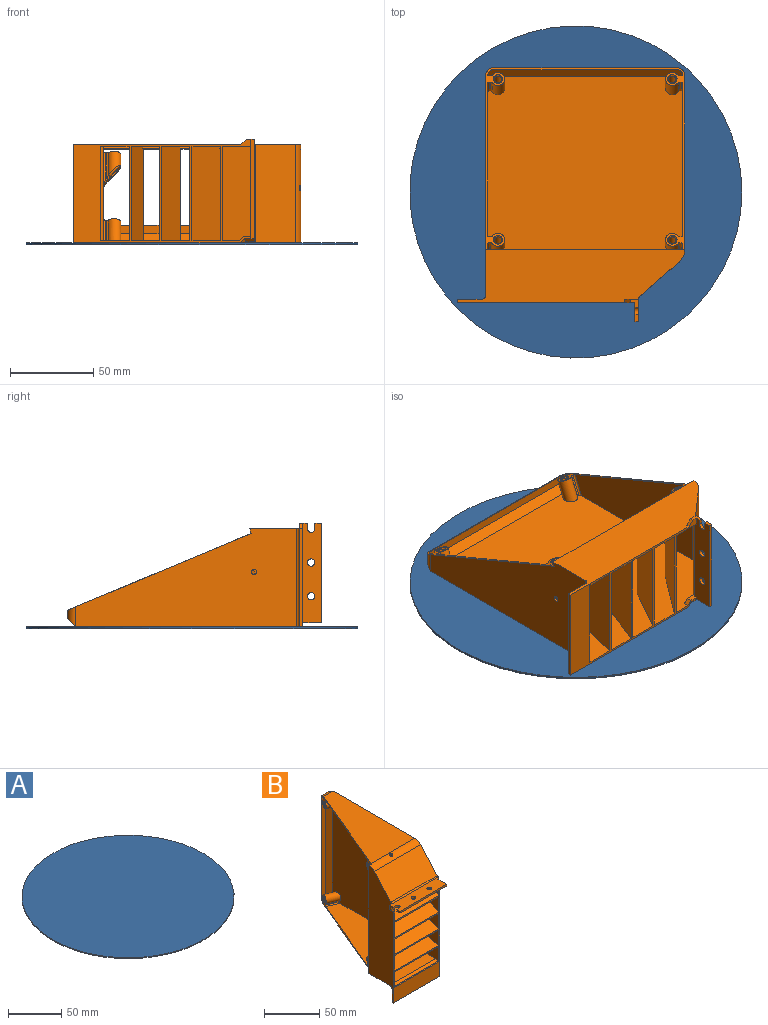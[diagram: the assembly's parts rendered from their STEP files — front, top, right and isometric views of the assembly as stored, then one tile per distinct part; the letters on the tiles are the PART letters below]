
ASSEMBLY  parts=2 mates=1
PART A: 3 faces, bbox 200x200x1 mm
  f0: cylinder r=100mm len=200mm, axis (0,0,-1), area 628.3mm2, adj f1,f2
  f1: plane 200x200mm, normal (0,0,1), area 31415.9mm2, adj f0
  f2: plane 200x200mm, normal (0,0,-1), area 31415.9mm2, adj f0
PART B: 134 faces, bbox 66.3x155.3x139.3 mm
  f0: plane 137.39x136.94mm, normal (1,0,0), area 15946.5mm2, adj f2,f23,f25,f38,f40,f42,f43,f44
  f1: plane 137x32mm, normal (-1,0,0), area 3430.7mm2, adj f2,f24,f26,f38,f39,f40,f42,f43
  f2: cylinder r=10mm len=59.06mm, axis (-1,0,0), area 492.2mm2, adj f0,f1,f22,f24,f25,f43,f132
  f3: cylinder r=8.8mm len=56.66mm, axis (-1,0,0), area 387.3mm2, adj f4,f5,f18,f22,f49,f53,f54,f58
  f4: plane 45.63x30.2mm, normal (1,0,0), area 599.4mm2, adj f3,f21,f37,f38,f51,f53,f58,f59
  f5: plane 138.4x121.59mm, normal (-1,0,0), area 15229.2mm2, adj f3,f17,f18,f19,f20,f38,f52,f56
  f6: plane 23.3x1.11mm, normal (0.92,-0.39,0), area 27.1mm2, adj f7,f24,f119,f127
  f7: plane 22.81x1.08mm, normal (-0.39,-0.92,0), area 26.4mm2, adj f6,f14,f119,f127
  f8: plane 34.04x30.2mm, normal (1,0,0), area 597.4mm2, adj f13,f38,f118,f124
  f9: plane 21.7x1.11mm, normal (0.92,-0.39,0), area 25.6mm2, adj f10,f24,f121,f123
  f10: plane 21.45x1.08mm, normal (-0.39,-0.92,0), area 25mm2, adj f9,f11,f121,f123
  f11: plane 30.2x28.5mm, normal (1,0,0), area 579.1mm2, adj f10,f38,f121,f123
  f12: plane 23.09x1.11mm, normal (0.92,-0.39,0), area 27.1mm2, adj f13,f24,f118,f124
  f13: plane 22.72x1.08mm, normal (-0.39,-0.92,0), area 26.4mm2, adj f8,f12,f118,f124
  f14: plane 39.59x30.2mm, normal (1,0,0), area 597.4mm2, adj f7,f38,f119,f127
  f15: plane 22.67x1.11mm, normal (0.92,-0.39,0), area 27.1mm2, adj f16,f17,f24,f120
  f16: plane 22.52x1.08mm, normal (-0.39,-0.92,0), area 26.3mm2, adj f15,f17,f50,f120
  f17: plane 128.03x56.82mm, normal (0,0,1), area 4787.5mm2, adj f5,f15,f16,f22,f50,f61,f82,f86
  f18: plane 99.87x51.06mm, normal (0,0,-1), area 3232.8mm2, adj f3,f5,f22,f94,f96
  f19: plane 8.51x3.56mm, normal (0,0,1), area 15mm2, adj f5,f60,f62,f84
  f20: plane 8.51x3.56mm, normal (0,0,-1), area 15mm2, adj f5,f60,f63,f98
  f21: plane 54.12x0.8mm, normal (0,1,0), area 43.3mm2, adj f4,f37,f51,f55
  f22: plane 120.88x111.58mm, normal (-0.92,0.39,0), area 597.5mm2, adj f2,f3,f17,f18,f24,f25,f41,f42
  f23: plane 5.65x0.54mm, normal (0,-1,0), area 2.9mm2, adj f0,f44,f129,f130
  f24: plane 120x2.75mm, normal (0.39,0.92,0), area 356.8mm2, adj f1,f2,f6,f9,f12,f15,f22,f42
  f25: plane 104.56x55.83mm, normal (0,0,1), area 3550.9mm2, adj f0,f2,f22,f48
  f26: plane 8.1x3.18mm, normal (0,1,0), area 20.7mm2, adj f1,f31,f36,f39
  f27: plane 3.18x2mm, normal (0,1,0), area 6.4mm2, adj f28,f35,f36,f37
  f28: plane 4.14x2mm, normal (-1,0,0), area 8.3mm2, adj f27,f29,f36,f37
  f29: plane 59.69x2mm, normal (0,-1,0), area 119.4mm2, adj f28,f30,f36,f37
  f30: plane 11.43x2mm, normal (1,0,0), area 22.9mm2, adj f29,f36,f37,f130
  f31: plane 4.92x4.87mm, normal (-1,0,0), area 15.6mm2, adj f26,f32,f36,f37,f38,f39
  f32: plane 3.18x2mm, normal (0,-1,0), area 6.4mm2, adj f31,f35,f36,f37
  f33: cylinder r=2.21mm len=4.42mm, axis (0,0,-1), area 27.8mm2, adj f36,f37
  f34: cylinder r=2.21mm len=4.42mm, axis (0,0,-1), area 27.8mm2, adj f36,f37
  f35: cylinder r=2.21mm len=4.42mm, axis (0,0,-1), area 13.9mm2, adj f27,f32,f36,f37
  f36: plane 61.69x13.43mm, normal (0,0,1), area 751.2mm2, adj f26,f27,f28,f29,f30,f31,f32,f33
  f37: plane 59.69x12.63mm, normal (0,0,-1), area 694.8mm2, adj f4,f21,f27,f28,f29,f30,f31,f32
  f38: plane 107x62.23mm, normal (0,-1,0), area 1515.5mm2, adj f0,f1,f4,f5,f8,f11,f14,f31
  f39: plane 3.18x3.18mm, normal (-0.71,0,-0.71), area 9mm2, adj f1,f26,f31,f38
  f40: plane 59.06x15mm, normal (0,1,0), area 885.8mm2, adj f0,f1,f46,f133
  f41: plane 110x5mm, normal (0,1,0), area 550mm2, adj f22,f45,f47,f48
  f42: plane 132.56x59.06mm, normal (0,0,-1), area 5194.7mm2, adj f0,f1,f22,f24,f46,f47,f131
  f43: plane 59.06x23.91mm, normal (0,-0.75,0.66), area 1878.7mm2, adj f0,f1,f2,f44
  f44: cylinder r=2mm len=59.06mm, axis (-1,0,0), area 100.5mm2, adj f0,f1,f23,f36,f43
  f45: plane 122.1x7.1mm, normal (0.71,0.71,0), area 833.4mm2, adj f0,f41,f47,f48
  f46: cylinder r=2mm len=59.06mm, axis (1,0,0), area 185.5mm2, adj f0,f1,f40,f42
  f47: cylinder r=5mm len=12.09mm, axis (1,0,0), area 67.1mm2, adj f22,f41,f42,f45
  f48: cylinder r=5mm len=12.09mm, axis (-1,0,0), area 67.1mm2, adj f22,f25,f41,f45
  f49: plane 23.5x1.11mm, normal (0.92,-0.39,0), area 27.6mm2, adj f3,f24,f53,f128
  f50: plane 30.2x24.17mm, normal (1,0,0), area 575.2mm2, adj f16,f17,f38,f61,f64,f120
  f51: plane 54.12x0.8mm, normal (0,0,-1), area 43.3mm2, adj f4,f21,f55,f59
  f52: plane 8.01x2.54mm, normal (0,1,0), area 17.1mm2, adj f5,f55,f56,f59
  f53: plane 23.39x1.08mm, normal (-0.39,-0.92,0), area 27.1mm2, adj f3,f4,f49,f128
  f54: plane 8.44x3mm, normal (0,0,-1), area 12.7mm2, adj f3,f22,f92
  f55: plane 5.47x3.2mm, normal (-1,0,0), area 15.9mm2, adj f21,f37,f38,f51,f52,f56,f59
  f56: plane 3.2x2.54mm, normal (-0.71,0,-0.71), area 11.5mm2, adj f5,f38,f52,f55
  f57: plane 110x5.01mm, normal (0,-1,0), area 550.5mm2, adj f22,f60,f62,f63
  f58: plane 56.66x23.91mm, normal (0,0.75,-0.66), area 1802.3mm2, adj f3,f4,f5,f59
  f59: cylinder r=3.2mm len=56.66mm, axis (-1,0,0), area 151.1mm2, adj f4,f5,f51,f52,f55,f58
  f60: plane 119.2x5.9mm, normal (-0.71,-0.71,0), area 705.9mm2, adj f5,f19,f20,f57,f62,f63
  f61: cylinder r=3.2mm len=56.66mm, axis (1,0,0), area 193.2mm2, adj f5,f17,f50,f64
  f62: cylinder r=3.8mm len=10.15mm, axis (1,0,0), area 45mm2, adj f19,f22,f57,f60,f84
  f63: cylinder r=3.8mm len=10.15mm, axis (-1,0,0), area 45mm2, adj f20,f22,f57,f60,f98
  f64: plane 56.66x1.2mm, normal (0,0,1), area 68mm2, adj f5,f38,f50,f61
  f65: plane 10.92x4.57mm, normal (0.39,0.92,0), area 12.5mm2, adj f5,f22,f97,f98
  f66: plane 12.47x5.22mm, normal (-0.39,-0.92,0), area 14.2mm2, adj f5,f22,f95,f96
  f67: cylinder r=4.2mm len=15.87mm, axis (-0.92,0.39,0), area 269mm2, adj f5,f22,f95,f97
  f68: cylinder r=2.2mm len=14.89mm, axis (-0.92,0.39,0), area 184.9mm2, adj f0,f115
  f69: plane 12.47x5.22mm, normal (-0.39,-0.92,0), area 14.2mm2, adj f5,f22,f85,f86
  f70: plane 10.92x4.57mm, normal (0.39,0.92,0), area 12.5mm2, adj f5,f22,f83,f84
  f71: cylinder r=4.2mm len=15.87mm, axis (-0.92,0.39,0), area 269mm2, adj f5,f22,f83,f85
  f72: cylinder r=2.2mm len=14.89mm, axis (-0.92,0.39,0), area 184.9mm2, adj f0,f113
  f73: cylinder r=2.2mm len=15.59mm, axis (-0.92,0.39,0), area 171.5mm2, adj f77,f116
  f74: plane 16.39x6.86mm, normal (0.39,0.92,0), area 18mm2, adj f22,f93,f94,f104
  f75: plane 16.39x6.86mm, normal (-0.39,-0.92,0), area 18mm2, adj f22,f91,f92,f100
  f76: cylinder r=4.2mm len=16.68mm, axis (-0.92,0.39,0), area 224.5mm2, adj f22,f91,f93,f102
  f77: plane 12.58x10.56mm, normal (0.59,-0.25,-0.77), area 39.5mm2, adj f3,f73,f99,f100,f101,f102,f103,f104
  f78: cylinder r=2.2mm len=15.59mm, axis (-0.92,0.39,0), area 171.5mm2, adj f82,f114
  f79: plane 16.39x6.86mm, normal (-0.39,-0.92,0), area 18mm2, adj f22,f89,f90,f111
  f80: plane 16.39x6.86mm, normal (0.39,0.92,0), area 18mm2, adj f22,f87,f88,f107
  f81: cylinder r=4.2mm len=16.68mm, axis (-0.92,0.39,0), area 224.5mm2, adj f22,f87,f89,f109
  f82: plane 12.29x10.27mm, normal (0.59,-0.25,0.77), area 40.9mm2, adj f17,f78,f106,f107,f108,f109,f110,f111
  f83: cylinder r=1mm len=11.09mm, axis (-0.92,0.39,0), area 11.2mm2, adj f5,f22,f70,f71
  f84: cylinder r=1mm len=11.31mm, axis (0.92,-0.39,0), area 17.9mm2, adj f5,f19,f22,f62,f70
  f85: cylinder r=1mm len=12.79mm, axis (-0.92,0.39,0), area 13mm2, adj f5,f22,f69,f71
  f86: cylinder r=1mm len=13.24mm, axis (-0.92,0.39,0), area 21.6mm2, adj f5,f17,f22,f69
  f87: cylinder r=1mm len=15.4mm, axis (-0.92,0.39,0), area 14.9mm2, adj f22,f80,f81,f108
  f88: cylinder r=1mm len=18.97mm, axis (0.92,-0.39,0), area 29.8mm2, adj f17,f22,f80,f106
  f89: cylinder r=1mm len=15.4mm, axis (-0.92,0.39,0), area 14.9mm2, adj f22,f79,f81,f110
  f90: cylinder r=1mm len=18.97mm, axis (-0.92,0.39,0), area 29.8mm2, adj f17,f22,f79,f112
  f91: cylinder r=1mm len=15.4mm, axis (-0.92,0.39,0), area 14.9mm2, adj f22,f75,f76,f101
  f92: cylinder r=1mm len=17.55mm, axis (-0.92,0.39,0), area 22.5mm2, adj f3,f22,f54,f75,f99
  f93: cylinder r=1mm len=15.4mm, axis (-0.92,0.39,0), area 14.9mm2, adj f22,f74,f76,f103
  f94: cylinder r=1mm len=20.8mm, axis (0.92,-0.39,0), area 30.2mm2, adj f3,f18,f22,f74,f105
  f95: cylinder r=1mm len=12.79mm, axis (-0.92,0.39,0), area 13mm2, adj f5,f22,f66,f67
  f96: cylinder r=1mm len=13.24mm, axis (-0.92,0.39,0), area 21.6mm2, adj f5,f18,f22,f66
  f97: cylinder r=1mm len=11.09mm, axis (-0.92,0.39,0), area 11.2mm2, adj f5,f22,f65,f67
  f98: cylinder r=1mm len=11.31mm, axis (0.92,-0.39,0), area 17.9mm2, adj f5,f20,f22,f63,f65
  f99: bspline ~2.13x1.4mm, area 1.8mm2, adj f3,f77,f92,f100
  f100: cylinder r=1mm len=2.14mm, axis (0.71,-0.3,0.64), area 2.6mm2, adj f75,f77,f99,f101
  f101: bspline ~3.51x2.72mm, area 4.2mm2, adj f77,f91,f100,f102
  f102: bspline ~8.43x8.42mm, area 34.2mm2, adj f76,f77,f101,f103
  f103: bspline ~2.74x2.72mm, area 4.2mm2, adj f77,f93,f102,f104
  f104: cylinder r=1mm len=1.82mm, axis (-0.71,0.3,-0.64), area 2.6mm2, adj f74,f77,f103,f105
  f105: bspline ~3.48x2.34mm, area 3.3mm2, adj f3,f77,f94,f104
  f106: bspline ~3.27x2.09mm, area 3.4mm2, adj f17,f82,f88,f107
  f107: cylinder r=1mm len=1.82mm, axis (0.71,-0.3,-0.64), area 2.6mm2, adj f80,f82,f106,f108
  f108: bspline ~2.74x2.72mm, area 4.2mm2, adj f82,f87,f107,f109
  f109: bspline ~8.43x8.42mm, area 34.2mm2, adj f81,f82,f108,f110
  f110: bspline ~3.51x2.72mm, area 4.2mm2, adj f82,f89,f109,f111
  f111: cylinder r=1mm len=2.14mm, axis (-0.71,0.3,0.64), area 2.6mm2, adj f79,f82,f110,f112
  f112: bspline ~2.77x2.54mm, area 3.4mm2, adj f17,f82,f90,f111
  f113: cone r=2.8mm half-angle=45deg, axis (-0.92,0.39,0), area 13.3mm2, adj f22,f72
  f114: cone r=2.2mm half-angle=45deg, axis (-0.92,0.39,0), area 13.3mm2, adj f22,f78
  f115: cone r=2.2mm half-angle=45deg, axis (-0.92,0.39,0), area 13.3mm2, adj f22,f68
  f116: cone r=2.8mm half-angle=45deg, axis (-0.92,0.39,0), area 13.3mm2, adj f22,f73
  f117: plane 55.11x1.38mm, normal (0,1,0), area 75.9mm2, adj f5,f24,f118,f119
  f118: plane 56.66x30.85mm, normal (0,0.49,-0.87), area 2005.4mm2, adj f5,f8,f12,f13,f38,f117
  f119: plane 56.66x30.85mm, normal (0,-0.49,0.87), area 2005.4mm2, adj f5,f6,f7,f14,f38,f117
  f120: plane 56.66x30.85mm, normal (0,0.23,-0.97), area 1795.1mm2, adj f5,f15,f16,f38,f50,f122
  f121: plane 56.66x30.85mm, normal (0,-0.23,0.97), area 1795.1mm2, adj f5,f9,f10,f11,f38,f122
  f122: plane 55.11x1.23mm, normal (0,1,0), area 68mm2, adj f5,f24,f120,f121
  f123: plane 56.66x30.85mm, normal (0,0.36,-0.93), area 1868.9mm2, adj f5,f9,f10,f11,f38,f125
  f124: plane 56.66x30.85mm, normal (0,-0.36,0.93), area 1868.9mm2, adj f5,f8,f12,f13,f38,f125
  f125: plane 55.11x1.28mm, normal (0,1,0), area 70.8mm2, adj f5,f24,f123,f124
  f126: plane 55.11x1.5mm, normal (0,1,0), area 82.6mm2, adj f5,f24,f127,f128
  f127: plane 56.66x30.85mm, normal (0,0.6,-0.8), area 2180.8mm2, adj f5,f6,f7,f14,f38,f126
  f128: plane 56.66x30.85mm, normal (0,-0.6,0.8), area 2180.8mm2, adj f4,f5,f38,f49,f53,f126
  f129: plane 3.37x2.54mm, normal (0.5,-0.71,0.5), area 6.2mm2, adj f0,f23,f38,f130
  f130: plane 5.94x2mm, normal (0.71,-0.71,0), area 15.6mm2, adj f23,f30,f36,f38,f129
  f131: cylinder r=1.59mm len=3.18mm, axis (0,0,-1), area 12mm2, adj f17,f42
  f132: cylinder r=1.59mm len=3.18mm, axis (0,0,1), area 13.4mm2, adj f2,f3
  f133: plane 59.06x2mm, normal (0,0,-1), area 118.1mm2, adj f0,f1,f38,f40
PLACE A t=(-4.1,-3,-1)mm
PLACE B rot(axis=(0,1,0),90deg) t=(31.51,-81.08,62.23)mm
MATE planar B.f0 <-> A.f0  axis (0,0,-1) through (0,0,0)mm
